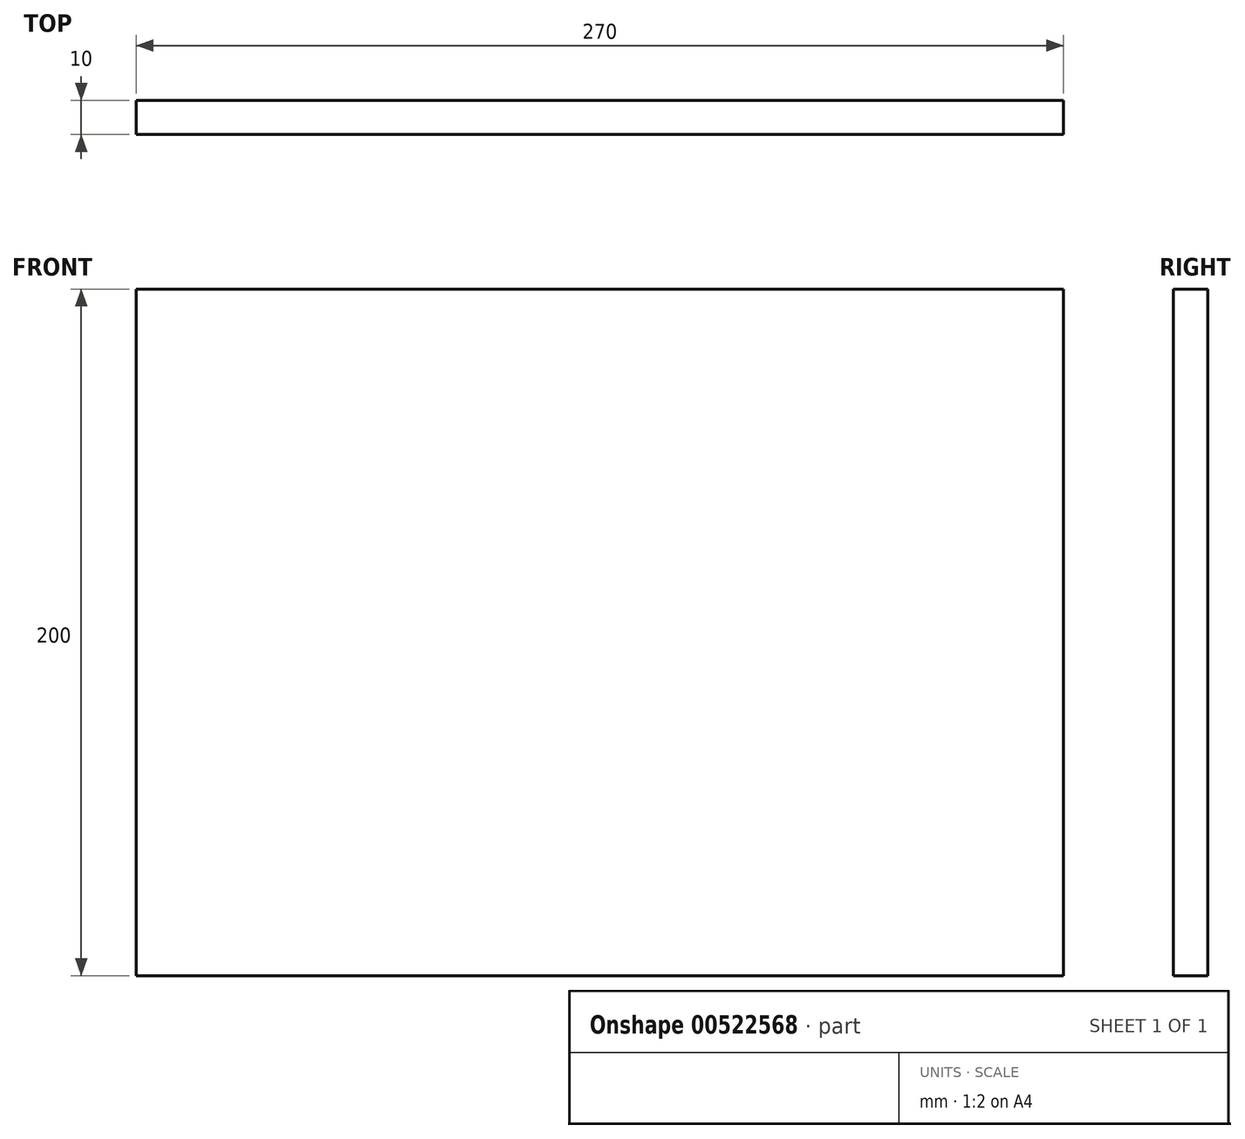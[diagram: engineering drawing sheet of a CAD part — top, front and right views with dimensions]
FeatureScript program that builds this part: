
annotation { "Feature Type Name" : "Feature", "Feature Type Description" : "" }
export const myFeature = defineFeature(function(context is Context, id is Id, definition is map)
    precondition{}
    {
        {
            var Q0;
            Q0=qCreatedBy(makeId("Front.planeOp"),FACE);
            var sketch = newSketch(context, id + "F0", { "sketchPlane" : qUnion([Q0])});
            skLineSegment(sketch, "E0.bottom", {"start": v(135, 100) * mm, "end": v(-135, 100) * mm});
            skLineSegment(sketch, "E0.top", {"start": v(135, -100) * mm, "end": v(-135, -100) * mm});
            skLineSegment(sketch, "E0.left", {"start": v(135, 100) * mm, "end": v(135, -100) * mm});
            skLineSegment(sketch, "E0.right", {"start": v(-135, 100) * mm, "end": v(-135, -100) * mm});
            skPoint(sketch, "E0.middle", {"position": v(0, 0) * mm});
            skSolve(sketch);
        }
        {
            var Q0;
            Q0=makeQuery(id+"F0.imprint","IMPRINT",FACE,{"disambiguationData":[TD([[makeQuery(id+"F0.imprint","IMPRINT",EDGE,{"derivedFrom":sQuery(id+"F0.wireOp",EDGE,"E0.bottom")}),1.0]])]});
            extrude(context, id + "F1", {"entities" : qUnion([Q0]), "depth" : 10 * mm, "offsetDistance" : 25 * mm});
        }
    });
